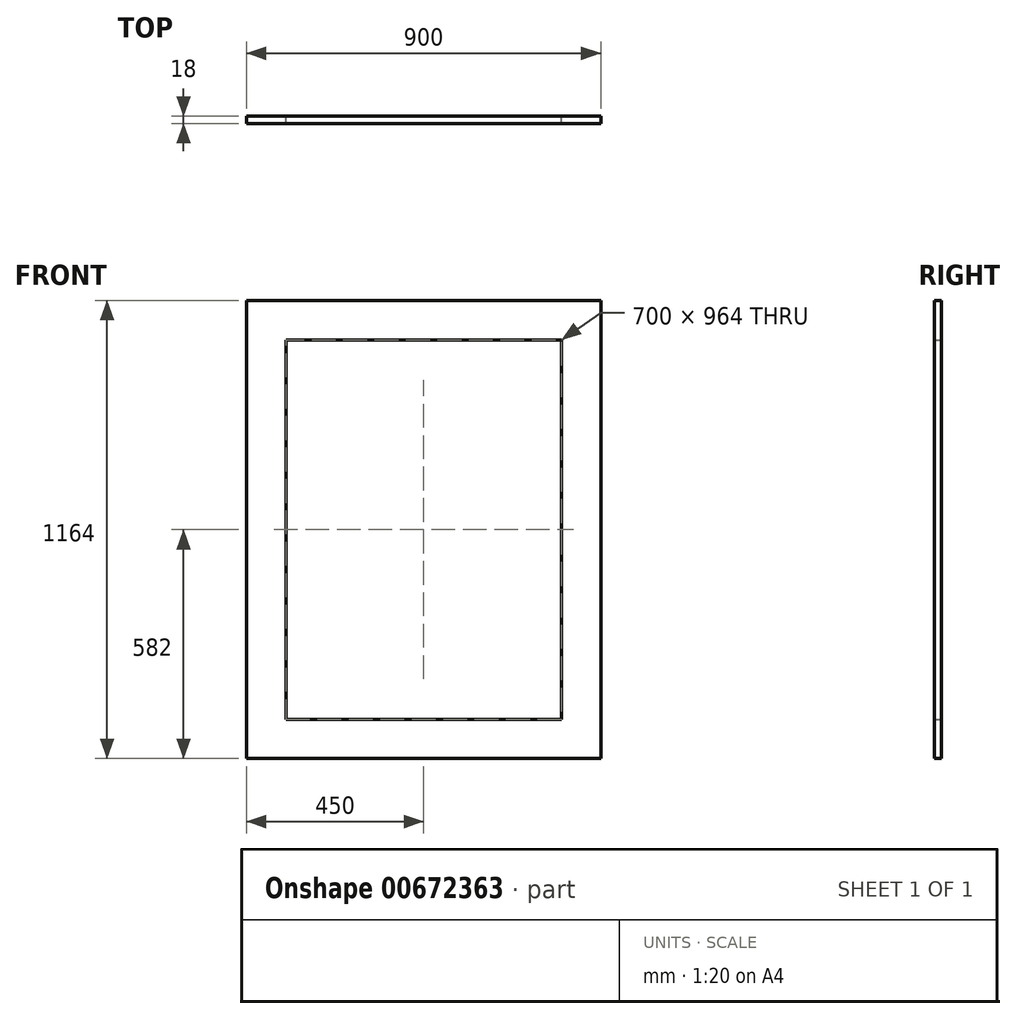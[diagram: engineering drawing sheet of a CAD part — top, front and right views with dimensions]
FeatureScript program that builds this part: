
annotation { "Feature Type Name" : "Feature", "Feature Type Description" : "" }
export const myFeature = defineFeature(function(context is Context, id is Id, definition is map)
    precondition{}
    {
        {
            var Q0;
            Q0=qCreatedBy(makeId("Front.planeOp"),FACE);
            var sketch = newSketch(context, id + "F0", { "sketchPlane" : qUnion([Q0])});
            skLineSegment(sketch, "E0.bottom", {"start": v(0, 0) * mm, "end": v(900, 0) * mm});
            skLineSegment(sketch, "E0.top", {"start": v(0, 1164) * mm, "end": v(900, 1164) * mm});
            skLineSegment(sketch, "E0.left", {"start": v(0, 0) * mm, "end": v(0, 1164) * mm});
            skLineSegment(sketch, "E0.right", {"start": v(900, 0) * mm, "end": v(900, 1164) * mm});
            skLineSegment(sketch, "E1.bottom", {"start": v(100, 1064) * mm, "end": v(800, 1064) * mm});
            skLineSegment(sketch, "E1.top", {"start": v(100, 100) * mm, "end": v(800, 100) * mm});
            skLineSegment(sketch, "E1.left", {"start": v(100, 1064) * mm, "end": v(100, 100) * mm});
            skLineSegment(sketch, "E1.right", {"start": v(800, 1064) * mm, "end": v(800, 100) * mm});
            skSolve(sketch);
        }
        {
            var Q0;
            Q0=makeQuery(id+"F0.imprint","IMPRINT",FACE,{"disambiguationData":[TD([[makeQuery(id+"F0.imprint","IMPRINT",EDGE,{"derivedFrom":sQuery(id+"F0.wireOp",EDGE,"E0.bottom")}),1.0]])]});
            extrude(context, id + "F1", {"entities" : qUnion([Q0]), "depth" : 18 * mm, "offsetDistance" : 25 * mm});
        }
    });
